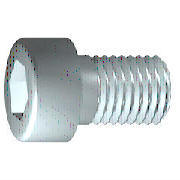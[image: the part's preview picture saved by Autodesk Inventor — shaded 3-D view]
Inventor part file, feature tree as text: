
AUTODESK INVENTOR PART (.ipt)
format: ipt  version: 2020 (Build 240168000, 168)  size: 197,120 bytes
history: native  units: mm (DEFAULTED — no unit token found)
features: sketch x2, extrude x1, plane x1, fillet x1
ambient origin geometry x7: Origin, YZ Plane, XY Plane, X Axis, Y Axis, Z Axis, Center Point
bodies: Solid1 (feature_tree)
feature tree (5):
  extrude  "슬롯"  Depth=8.0mm
  plane  "Work Plane1"
  fillet  "Fillet2"  Radius=0.49086mm
  sketch  "스케치1"
  sketch  "스케치2"
